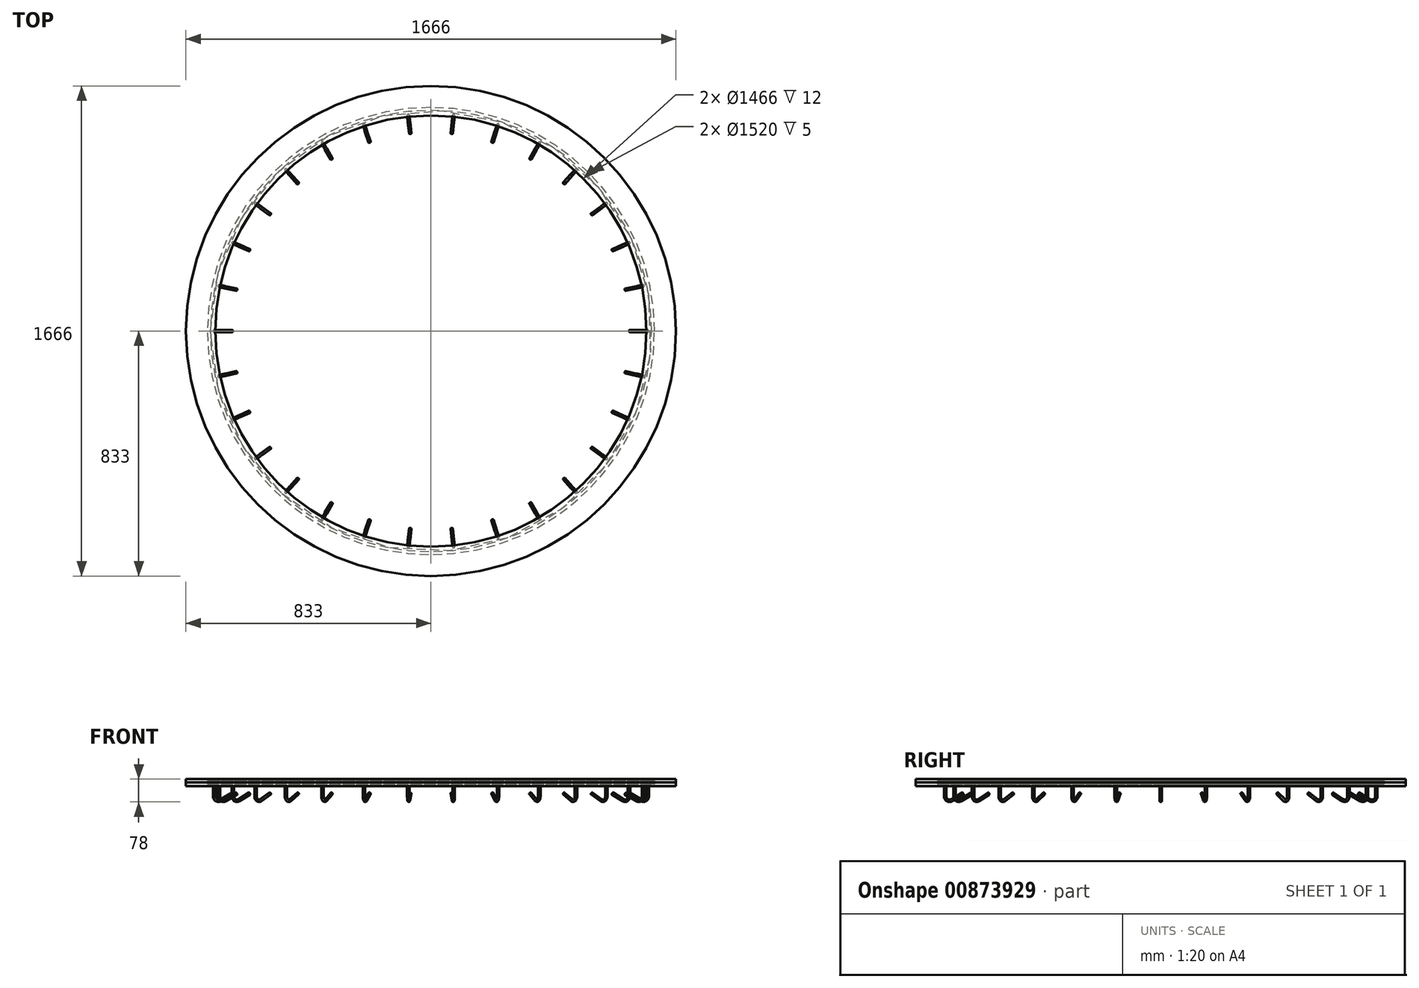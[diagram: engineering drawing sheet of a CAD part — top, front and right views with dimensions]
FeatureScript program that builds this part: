
annotation { "Feature Type Name" : "Feature", "Feature Type Description" : "" }
export const myFeature = defineFeature(function(context is Context, id is Id, definition is map)
    precondition{}
    {
        {
            var Q0;
            Q0=qCreatedBy(makeId("Front.planeOp"),FACE);
            var sketch = newSketch(context, id + "F0", { "sketchPlane" : qUnion([Q0])});
            skLineSegment(sketch, "E0", {"start": v(0, 0) * mm, "end": v(833, 0) * mm, "construction": true});
            skLineSegment(sketch, "E1.bottom", {"start": v(833, 0) * mm, "end": v(760, 0) * mm});
            skLineSegment(sketch, "E1.top", {"start": v(833, -12) * mm, "end": v(733, -12) * mm});
            skLineSegment(sketch, "E1.left", {"start": v(833, 0) * mm, "end": v(833, -12) * mm});
            skLineSegment(sketch, "E1.right", {"start": v(733, 0) * mm, "end": v(733, -12) * mm});
            skLineSegment(sketch, "E2.MirrorCS", {"start": v(833, 12) * mm, "end": v(733, 12) * mm});
            skLineSegment(sketch, "E3.MirrorCS", {"start": v(733, 0) * mm, "end": v(733, 12) * mm});
            skLineSegment(sketch, "E4.MirrorCS", {"start": v(833, 0) * mm, "end": v(833, 12) * mm});
            skPoint(sketch, "E5", {"position": v(760, 0) * mm});
            skLineSegment(sketch, "E6.bottom", {"start": v(750, 5) * mm, "end": v(760, 5) * mm});
            skLineSegment(sketch, "E6.top", {"start": v(750, -5) * mm, "end": v(760, -5) * mm});
            skLineSegment(sketch, "E6.left", {"start": v(750, 5) * mm, "end": v(750, -5) * mm});
            skLineSegment(sketch, "E6.right", {"start": v(760, 5) * mm, "end": v(760, -5) * mm});
            skLineSegment(sketch, "E7.trimOffspring", {"start": v(750, 0) * mm, "end": v(733, 0) * mm});
            skLineSegment(sketch, "E8", {"start": v(750, 5) * mm, "end": v(760, -5) * mm, "construction": true});
            skCircle(sketch, "E9", {"center": v(755, 0) * mm, "radius": 5 * mm});
            skLineSegment(sketch, "E10", {"start": v(0, 0) * mm, "end": v(0, 141.25) * mm, "construction": true});
            skSolve(sketch);
        }
        {
            var Q0;
            {var subQ2=sQuery(id+"F0.wireOp",EDGE,"E1.bottom");Q0=makeQuery(id+"F0.imprint","IMPRINT",FACE,{"disambiguationData":[TD([[makeQuery(id+"F0.imprint","IMPRINT",EDGE,{"derivedFrom":subQ2}),1.0]])]});}
            var Q1;
            Q1=sQuery(id+"F0.wireOp",EDGE,"E10");
            revolve(context, id + "F1", {"surfaceOperationType" : NewSurfaceOperationType.NEW, "entities" : qUnion([Q0]), "axis" : qUnion([Q1]), "revolveType" : RevolveType.FULL});
        }
        {
            var Q0;
            {var subQ0=sQuery(id+"F0.wireOp",EDGE,"E9");var subQ2=makeQuery(id+"F0.imprint","INTERSECT",VERTEX,{"derivedFrom":[sQuery(id+"F0.wireOp",EDGE,"E6.bottom"),subQ0]});Q0=makeQuery(id+"F0.imprint","IMPRINT",FACE,{"disambiguationData":[TD([[makeQuery(id+"F0.imprint","IMPRINT",EDGE,{"disambiguationData":[TD([[subQ2,1.0]])],"derivedFrom":subQ0}),1.0]])]});}
            var Q1;
            Q1=sQuery(id+"F0.wireOp",EDGE,"E10");
            revolve(context, id + "F2", {"surfaceOperationType" : NewSurfaceOperationType.NEW, "entities" : qUnion([Q0]), "axis" : qUnion([Q1]), "revolveType" : RevolveType.FULL});
        }
        {
            var Q0;
            {var subQ1=sQuery(id+"F0.wireOp",EDGE,"E1.bottom");Q0=makeQuery(id+"F0.imprint","IMPRINT",FACE,{"disambiguationData":[TD([[makeQuery(id+"F0.imprint","IMPRINT",EDGE,{"derivedFrom":subQ1}),-1.0]])]});}
            var Q1;
            Q1=sQuery(id+"F0.wireOp",EDGE,"E10");
            revolve(context, id + "F3", {"surfaceOperationType" : NewSurfaceOperationType.NEW, "entities" : qUnion([Q0]), "axis" : qUnion([Q1]), "revolveType" : RevolveType.FULL});
        }
        {
            var Q0;
            Q0=makeQuery(id+"F1.opRevolve","SWEPT_FACE",FACE,{"disambiguationData":[OSD([sQuery(id+"F0.wireOp",EDGE,"E1.top")])]});
            var sketch = newSketch(context, id + "F4", { "sketchPlane" : qUnion([Q0])});
            skCircle(sketch, "E11", {"center": v(737, 0) * mm, "radius": 4 * mm});
            skLineSegment(sketch, "E12", {"start": v(737, 0) * mm, "end": v(733, 0) * mm, "construction": true});
            skSolve(sketch);
        }
        {
            var Q0;
            Q0=qCreatedBy(makeId("Front.planeOp"),FACE);
            var sketch = newSketch(context, id + "F5", { "sketchPlane" : qUnion([Q0])});
            skLineSegment(sketch, "E13", {"start": v(737, -12) * mm, "end": v(737, -47) * mm});
            skLineSegment(sketch, "E14", {"start": v(714.5, -60) * mm, "end": v(675.53, -37.5) * mm});
            skPoint(sketch, "E15.visualSharp", {"position": v(737, -72.98) * mm});
            skArc(sketch, "E15.filletArc", {"start": v(714.5, -60) * mm, "mid": v(729.5, -60) * mm, "end": v(737, -47) * mm});
            skSolve(sketch);
        }
        {
            var Q0;
            Q0=makeQuery(id+"F4.imprint","IMPRINT",FACE,{"disambiguationData":[TD([[makeQuery(id+"F4.imprint","IMPRINT",EDGE,{"derivedFrom":sQuery(id+"F4.wireOp",EDGE,"E11")}),1.0]])]});
            var Q1;
            Q1=sQuery(id+"F5.wireOp",EDGE,"E13");
            var Q2;
            Q2=sQuery(id+"F5.wireOp",EDGE,"E15.filletArc");
            var Q3;
            Q3=sQuery(id+"F5.wireOp",EDGE,"E14");
            sweep(context, id + "F6", {"profiles" : qUnion([Q0]), "path" : qUnion([Q1, Q2, Q3])});
        }
        {
            var Q0;
            Q0=makeQuery(id+"F6.opSweep","SWEPT_BODY",BODY,{"disambiguationData":[OSD([sQuery(id+"F4.wireOp",EDGE,"E11"),sQuery(id+"F5.wireOp",EDGE,"E14")])]});
            var Q1;
            Q1=sQuery(id+"F0.wireOp",EDGE,"E10");
            circularPattern(context, id + "F7", {"entities" : qUnion([Q0]), "axis" : qUnion([Q1]), "angle" : 360 * degree, "instanceCount" : 30, "equalSpace" : true});
        }
    });
